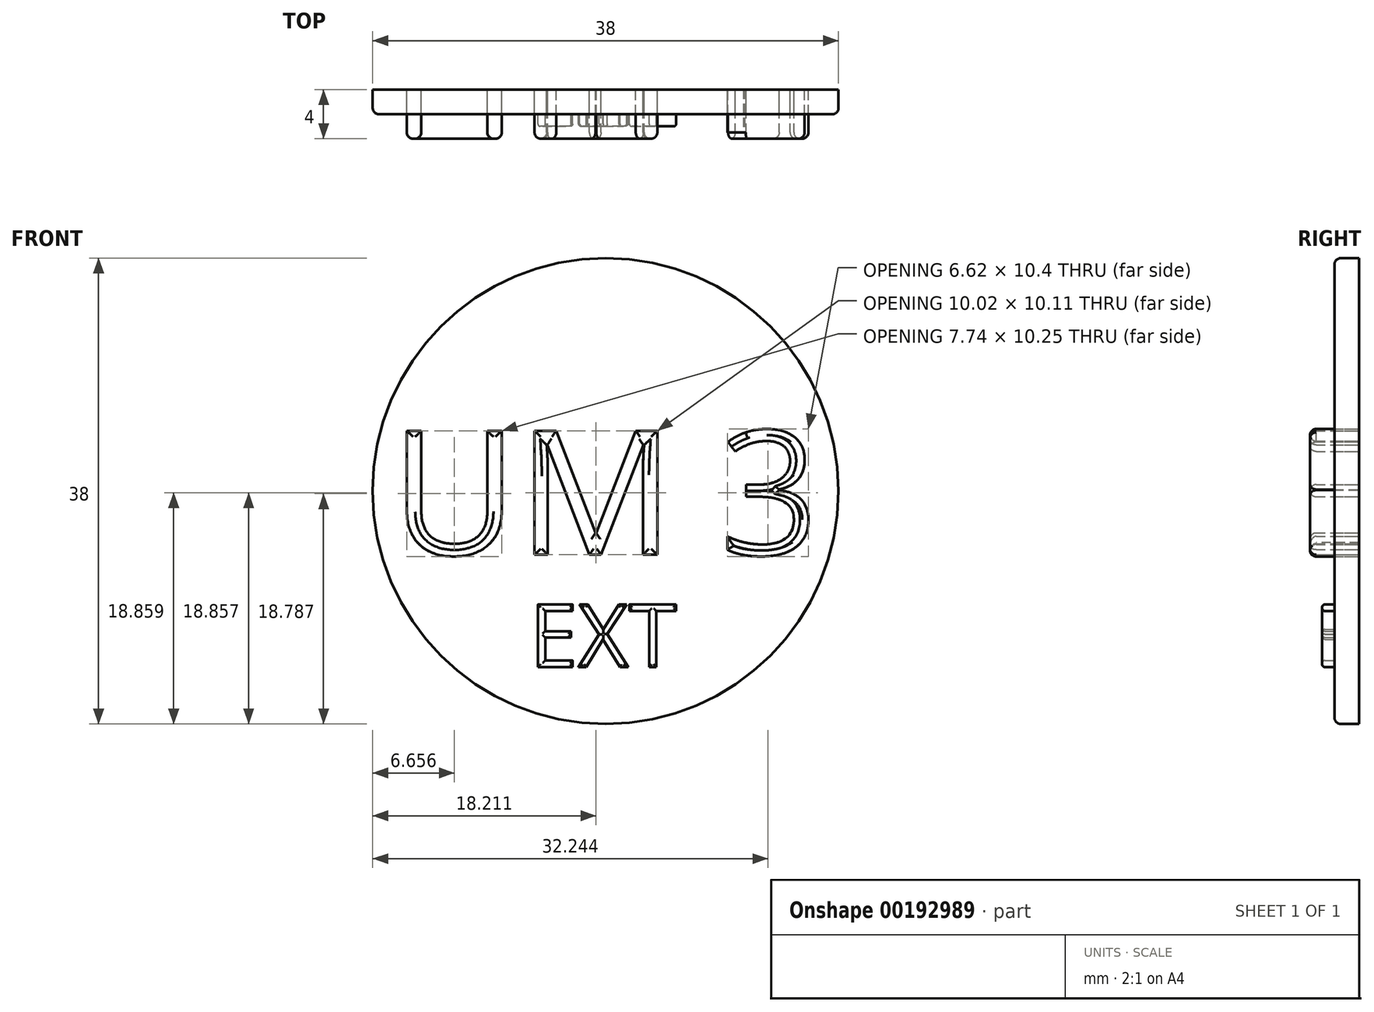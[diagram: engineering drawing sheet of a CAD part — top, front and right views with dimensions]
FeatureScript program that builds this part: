
annotation { "Feature Type Name" : "Feature", "Feature Type Description" : "" }
export const myFeature = defineFeature(function(context is Context, id is Id, definition is map)
    precondition{}
    {
        {
            var Q0;
            Q0=qCreatedBy(makeId("Front.planeOp"),FACE);
            var sketch = newSketch(context, id + "F0", { "sketchPlane" : qUnion([Q0])});
            skCircle(sketch, "E0", {"center": v(0, 0) * mm, "radius": 19 * mm});
            skText(sketch, "E1", { "text": "UM 3", "fontName": "OpenSans-Regular.ttf"});
            const initialGuessF0  = {"E1": [-0.0175, -0.0052, 1, 0, 0.0102]};
            skSetInitialGuess(sketch, initialGuessF0);
            skSolve(sketch);
        }
        {
            var Q0;
            Q0=makeQuery(id+"F0.imprint","IMPRINT",FACE,{"disambiguationData":[TD([[makeQuery(id+"F0.imprint","IMPRINT",EDGE,{"derivedFrom":sQuery(id+"F0.wireOp",EDGE,"E1.sketch_text.stroke-32")}),-1.0]])]});
            var Q1;
            Q1=makeQuery(id+"F0.imprint","IMPRINT",FACE,{"disambiguationData":[TD([[makeQuery(id+"F0.imprint","IMPRINT",EDGE,{"derivedFrom":sQuery(id+"F0.wireOp",EDGE,"E1.sketch_text.stroke-14")}),-1.0]])]});
            var Q2;
            Q2=makeQuery(id+"F0.imprint","IMPRINT",FACE,{"disambiguationData":[TD([[makeQuery(id+"F0.imprint","IMPRINT",EDGE,{"derivedFrom":sQuery(id+"F0.wireOp",EDGE,"E1.sketch_text.stroke-0")}),-1.0]])]});
            extrude(context, id + "F1", {"entities" : qUnion([Q0, Q1, Q2]), "depth" : 4 * mm});
        }
        {
            var Q0;
            Q0=makeQuery(id+"F0.imprint","IMPRINT",FACE,{"disambiguationData":[TD([[makeQuery(id+"F0.imprint","IMPRINT",EDGE,{"derivedFrom":sQuery(id+"F0.wireOp",EDGE,"E0")}),1.0]])]});
            extrude(context, id + "F2", {"entities" : qUnion([Q0]), "depth" : 2 * mm});
        }
        {
            var Q0;
            Q0=makeQuery(id+"F1.opExtrude","CAP_FACE",FACE,{"disambiguationData":[OSD([sQuery(id+"F0.wireOp",EDGE,"E1.sketch_text.stroke-0"),sQuery(id+"F0.wireOp",EDGE,"E1.sketch_text.stroke-1"),sQuery(id+"F0.wireOp",EDGE,"E1.sketch_text.stroke-2"),sQuery(id+"F0.wireOp",EDGE,"E1.sketch_text.stroke-3"),sQuery(id+"F0.wireOp",EDGE,"E1.sketch_text.stroke-4"),sQuery(id+"F0.wireOp",EDGE,"E1.sketch_text.stroke-5"),sQuery(id+"F0.wireOp",EDGE,"E1.sketch_text.stroke-6"),sQuery(id+"F0.wireOp",EDGE,"E1.sketch_text.stroke-7"),sQuery(id+"F0.wireOp",EDGE,"E1.sketch_text.stroke-8"),sQuery(id+"F0.wireOp",EDGE,"E1.sketch_text.stroke-9"),sQuery(id+"F0.wireOp",EDGE,"E1.sketch_text.stroke-10"),sQuery(id+"F0.wireOp",EDGE,"E1.sketch_text.stroke-11"),sQuery(id+"F0.wireOp",EDGE,"E1.sketch_text.stroke-12"),sQuery(id+"F0.wireOp",EDGE,"E1.sketch_text.stroke-13")])],"isStart":false});
            var Q1;
            Q1=makeQuery(id+"F1.opExtrude","CAP_FACE",FACE,{"disambiguationData":[OSD([sQuery(id+"F0.wireOp",EDGE,"E1.sketch_text.stroke-14"),sQuery(id+"F0.wireOp",EDGE,"E1.sketch_text.stroke-15"),sQuery(id+"F0.wireOp",EDGE,"E1.sketch_text.stroke-16"),sQuery(id+"F0.wireOp",EDGE,"E1.sketch_text.stroke-17"),sQuery(id+"F0.wireOp",EDGE,"E1.sketch_text.stroke-18"),sQuery(id+"F0.wireOp",EDGE,"E1.sketch_text.stroke-19"),sQuery(id+"F0.wireOp",EDGE,"E1.sketch_text.stroke-20"),sQuery(id+"F0.wireOp",EDGE,"E1.sketch_text.stroke-21"),sQuery(id+"F0.wireOp",EDGE,"E1.sketch_text.stroke-22"),sQuery(id+"F0.wireOp",EDGE,"E1.sketch_text.stroke-23"),sQuery(id+"F0.wireOp",EDGE,"E1.sketch_text.stroke-24"),sQuery(id+"F0.wireOp",EDGE,"E1.sketch_text.stroke-25"),sQuery(id+"F0.wireOp",EDGE,"E1.sketch_text.stroke-26"),sQuery(id+"F0.wireOp",EDGE,"E1.sketch_text.stroke-27"),sQuery(id+"F0.wireOp",EDGE,"E1.sketch_text.stroke-28"),sQuery(id+"F0.wireOp",EDGE,"E1.sketch_text.stroke-29"),sQuery(id+"F0.wireOp",EDGE,"E1.sketch_text.stroke-30"),sQuery(id+"F0.wireOp",EDGE,"E1.sketch_text.stroke-31")])],"isStart":false});
            var Q2;
            Q2=makeQuery(id+"F1.opExtrude","CAP_FACE",FACE,{"disambiguationData":[OSD([sQuery(id+"F0.wireOp",EDGE,"E1.sketch_text.stroke-32"),sQuery(id+"F0.wireOp",EDGE,"E1.sketch_text.stroke-33"),sQuery(id+"F0.wireOp",EDGE,"E1.sketch_text.stroke-34"),sQuery(id+"F0.wireOp",EDGE,"E1.sketch_text.stroke-35"),sQuery(id+"F0.wireOp",EDGE,"E1.sketch_text.stroke-36"),sQuery(id+"F0.wireOp",EDGE,"E1.sketch_text.stroke-37"),sQuery(id+"F0.wireOp",EDGE,"E1.sketch_text.stroke-38"),sQuery(id+"F0.wireOp",EDGE,"E1.sketch_text.stroke-39"),sQuery(id+"F0.wireOp",EDGE,"E1.sketch_text.stroke-40"),sQuery(id+"F0.wireOp",EDGE,"E1.sketch_text.stroke-41"),sQuery(id+"F0.wireOp",EDGE,"E1.sketch_text.stroke-42"),sQuery(id+"F0.wireOp",EDGE,"E1.sketch_text.stroke-43"),sQuery(id+"F0.wireOp",EDGE,"E1.sketch_text.stroke-44"),sQuery(id+"F0.wireOp",EDGE,"E1.sketch_text.stroke-45"),sQuery(id+"F0.wireOp",EDGE,"E1.sketch_text.stroke-46"),sQuery(id+"F0.wireOp",EDGE,"E1.sketch_text.stroke-47"),sQuery(id+"F0.wireOp",EDGE,"E1.sketch_text.stroke-48"),sQuery(id+"F0.wireOp",EDGE,"E1.sketch_text.stroke-49"),sQuery(id+"F0.wireOp",EDGE,"E1.sketch_text.stroke-50"),sQuery(id+"F0.wireOp",EDGE,"E1.sketch_text.stroke-51"),sQuery(id+"F0.wireOp",EDGE,"E1.sketch_text.stroke-52"),sQuery(id+"F0.wireOp",EDGE,"E1.sketch_text.stroke-53"),sQuery(id+"F0.wireOp",EDGE,"E1.sketch_text.stroke-54"),sQuery(id+"F0.wireOp",EDGE,"E1.sketch_text.stroke-55"),sQuery(id+"F0.wireOp",EDGE,"E1.sketch_text.stroke-56"),sQuery(id+"F0.wireOp",EDGE,"E1.sketch_text.stroke-57"),sQuery(id+"F0.wireOp",EDGE,"E1.sketch_text.stroke-58"),sQuery(id+"F0.wireOp",EDGE,"E1.sketch_text.stroke-59")])],"isStart":false});
            fillet(context, id + "F3", {"entities" : qUnion([Q0, Q1, Q2]), "radius" : 0.5 * mm, "tangentPropagation" : true, "allowEdgeOverflow" : false});
        }
        {
            var Q0;
            Q0=makeQuery(id+"F2.opExtrude","CAP_EDGE",EDGE,{"disambiguationData":[OSD([sQuery(id+"F0.wireOp",EDGE,"E0")])],"isStart":false});
            fillet(context, id + "F4", {"entities" : qUnion([Q0]), "radius" : 0.5 * mm, "tangentPropagation" : true, "allowEdgeOverflow" : false});
        }
        {
            var Q0;
            Q0=qCreatedBy(makeId("Front.planeOp"),FACE);
            var sketch = newSketch(context, id + "F5", { "sketchPlane" : qUnion([Q0])});
            skText(sketch, "E2", { "text": "EXT", "fontName": "OpenSans-Regular.ttf"});
            const initialGuessF5  = {"E2": [-0.00622, -0.01436, 1, 0, 0.00514]};
            skSetInitialGuess(sketch, initialGuessF5);
            skSolve(sketch);
        }
        {
            var Q0;
            Q0 = qSketchRegion(id + "F5", true);
            extrude(context, id + "F6", {"entities" : qUnion([Q0]), "operationType" : NewBodyOperationType.ADD, "depth" : 3 * mm});
        }
        {
            var Q0;
            Q0=makeQuery(id+"F6.opExtrude","CAP_FACE",FACE,{"disambiguationData":[OSD([sQuery(id+"F5.wireOp",EDGE,"E2.sketch_text.stroke-0"),sQuery(id+"F5.wireOp",EDGE,"E2.sketch_text.stroke-1"),sQuery(id+"F5.wireOp",EDGE,"E2.sketch_text.stroke-2"),sQuery(id+"F5.wireOp",EDGE,"E2.sketch_text.stroke-3"),sQuery(id+"F5.wireOp",EDGE,"E2.sketch_text.stroke-4"),sQuery(id+"F5.wireOp",EDGE,"E2.sketch_text.stroke-5"),sQuery(id+"F5.wireOp",EDGE,"E2.sketch_text.stroke-6"),sQuery(id+"F5.wireOp",EDGE,"E2.sketch_text.stroke-7"),sQuery(id+"F5.wireOp",EDGE,"E2.sketch_text.stroke-8"),sQuery(id+"F5.wireOp",EDGE,"E2.sketch_text.stroke-9"),sQuery(id+"F5.wireOp",EDGE,"E2.sketch_text.stroke-10"),sQuery(id+"F5.wireOp",EDGE,"E2.sketch_text.stroke-11")])],"isStart":false});
            var Q1;
            Q1=makeQuery(id+"F6.opExtrude","CAP_FACE",FACE,{"disambiguationData":[OSD([sQuery(id+"F5.wireOp",EDGE,"E2.sketch_text.stroke-12"),sQuery(id+"F5.wireOp",EDGE,"E2.sketch_text.stroke-13"),sQuery(id+"F5.wireOp",EDGE,"E2.sketch_text.stroke-14"),sQuery(id+"F5.wireOp",EDGE,"E2.sketch_text.stroke-15"),sQuery(id+"F5.wireOp",EDGE,"E2.sketch_text.stroke-16"),sQuery(id+"F5.wireOp",EDGE,"E2.sketch_text.stroke-17"),sQuery(id+"F5.wireOp",EDGE,"E2.sketch_text.stroke-18"),sQuery(id+"F5.wireOp",EDGE,"E2.sketch_text.stroke-19"),sQuery(id+"F5.wireOp",EDGE,"E2.sketch_text.stroke-20"),sQuery(id+"F5.wireOp",EDGE,"E2.sketch_text.stroke-21"),sQuery(id+"F5.wireOp",EDGE,"E2.sketch_text.stroke-22"),sQuery(id+"F5.wireOp",EDGE,"E2.sketch_text.stroke-23")])],"isStart":false});
            var Q2;
            Q2=makeQuery(id+"F6.opExtrude","CAP_FACE",FACE,{"disambiguationData":[OSD([sQuery(id+"F5.wireOp",EDGE,"E2.sketch_text.stroke-24"),sQuery(id+"F5.wireOp",EDGE,"E2.sketch_text.stroke-25"),sQuery(id+"F5.wireOp",EDGE,"E2.sketch_text.stroke-26"),sQuery(id+"F5.wireOp",EDGE,"E2.sketch_text.stroke-27"),sQuery(id+"F5.wireOp",EDGE,"E2.sketch_text.stroke-28"),sQuery(id+"F5.wireOp",EDGE,"E2.sketch_text.stroke-29"),sQuery(id+"F5.wireOp",EDGE,"E2.sketch_text.stroke-30"),sQuery(id+"F5.wireOp",EDGE,"E2.sketch_text.stroke-31")])],"isStart":false});
            fillet(context, id + "F7", {"entities" : qUnion([Q0, Q1, Q2]), "radius" : 0.2 * mm, "tangentPropagation" : true, "allowEdgeOverflow" : false});
        }
    });
